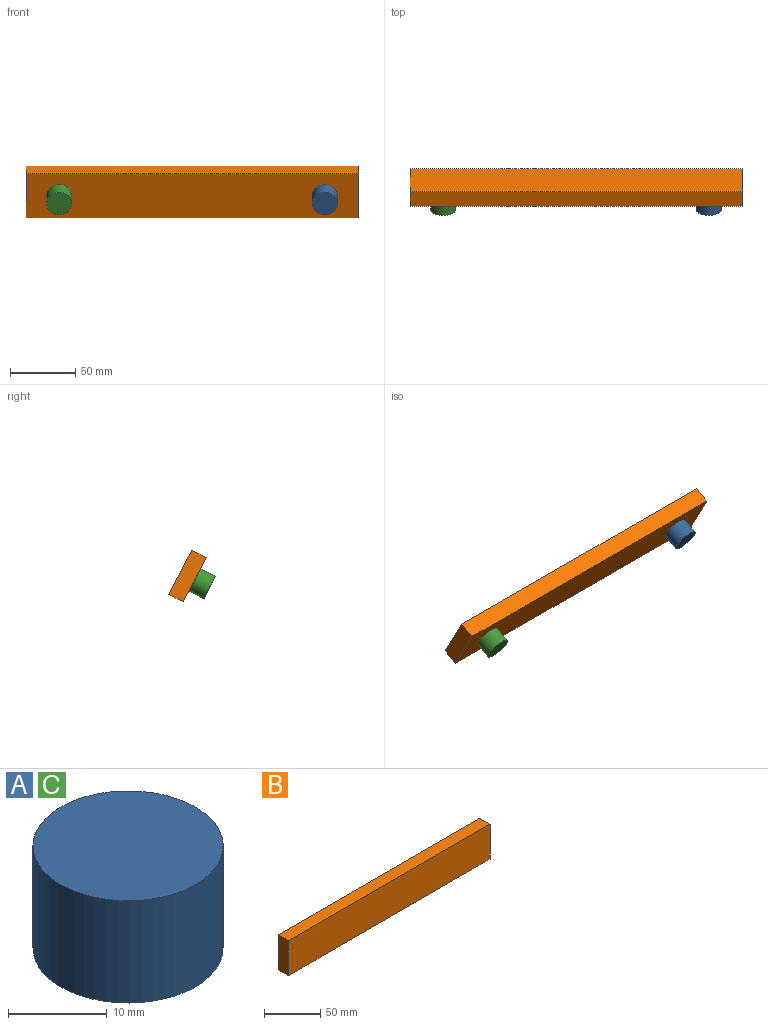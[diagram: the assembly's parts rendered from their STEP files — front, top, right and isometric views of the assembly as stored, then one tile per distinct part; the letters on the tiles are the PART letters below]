
ASSEMBLY  parts=3 mates=2
PART A: 3 faces, bbox 19.3x19.3x12.7 mm
  f0: cylinder r=9.65mm len=19.3mm, axis (0,0,-1), area 770.2mm2, adj f1,f2
  f1: plane 19.3x19.3mm, normal (0,0,1), area 292.7mm2, adj f0
  f2: plane 19.3x19.3mm, normal (0,0,-1), area 292.7mm2, adj f0
PART B: 6 faces, bbox 254x12.7x38.1 mm
  f0: plane 254x12.7mm, normal (0,0,1), area 3225.8mm2, adj f1,f3,f4,f5
  f1: plane 38.1x12.7mm, normal (-1,0,0), area 483.9mm2, adj f0,f2,f4,f5
  f2: plane 254x12.7mm, normal (0,0,-1), area 3225.8mm2, adj f1,f3,f4,f5
  f3: plane 38.1x12.7mm, normal (1,0,0), area 483.9mm2, adj f0,f2,f4,f5
  f4: plane 254x38.1mm, normal (0,-1,0), area 9677.4mm2, adj f0,f1,f2,f3
  f5: plane 254x38.1mm, normal (0,1,0), area 9677.4mm2, adj f0,f1,f2,f3
PART C: same geometry as A
PLACE A rot(axis=(-1,0,0),62.5deg) t=(-12.57,173.73,112.82)mm
PLACE B rot(axis=(1,0,0),27.5deg) t=(-171.31,248.26,24.76)mm
PLACE C rot(axis=(-1,0,0),62.5deg) t=(-215.77,173.73,112.82)mm
MATE fastened B.f4 <-> A.f0  axis (0,-0.89,-0.46) through (-40.91,214.01,63.01)mm
MATE fastened C.f0 <-> B.f4  axis (0,0.89,0.46) through (-244.11,214.01,63.01)mm
